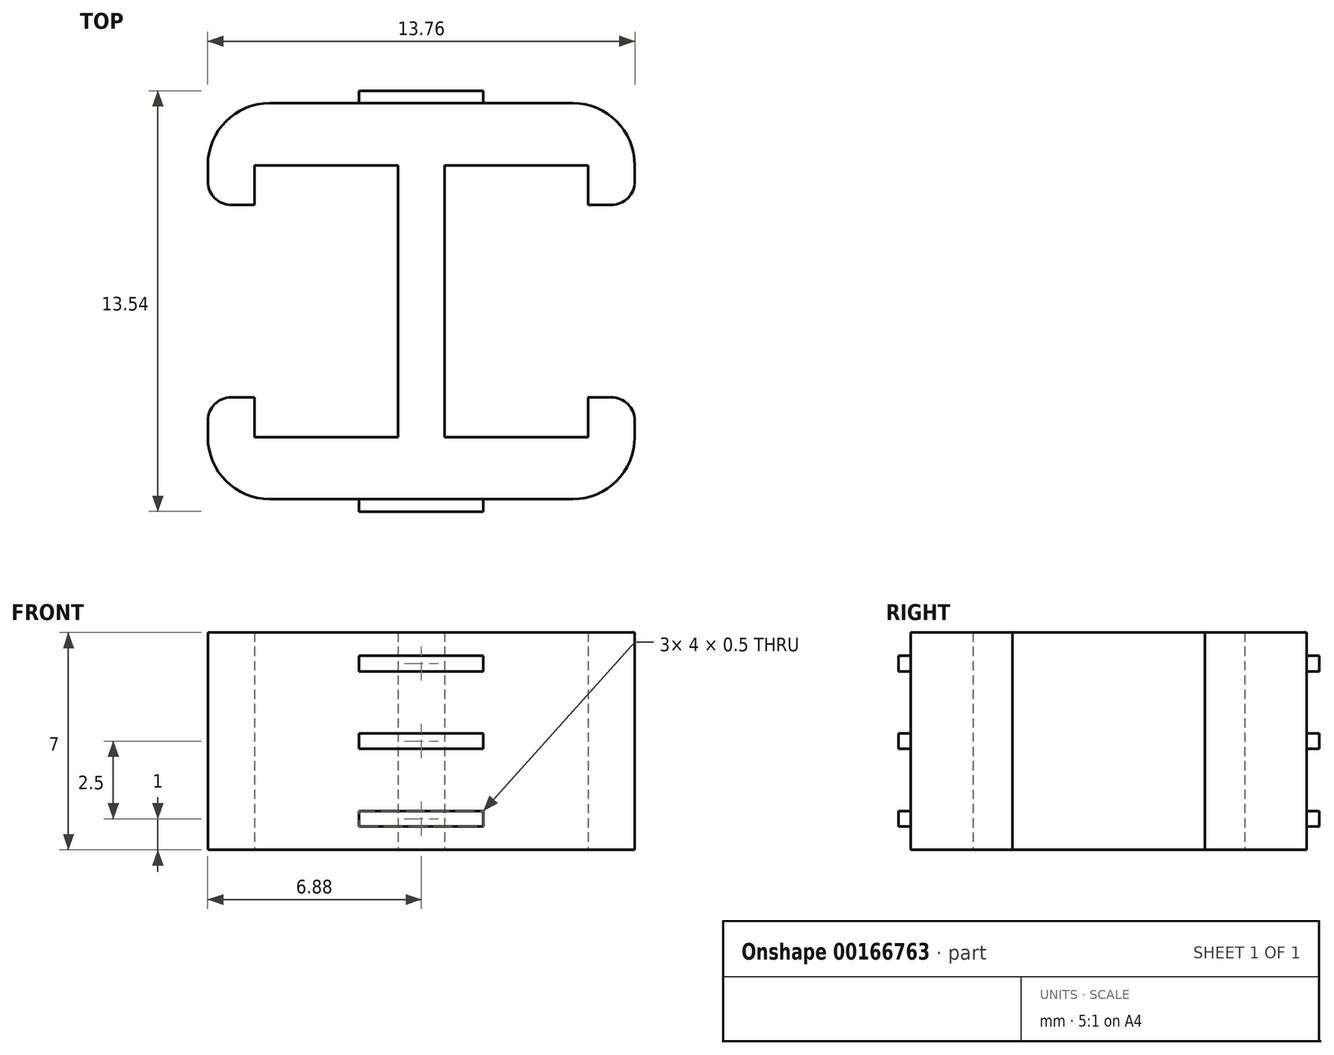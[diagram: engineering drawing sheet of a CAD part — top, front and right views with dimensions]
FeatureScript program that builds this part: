
annotation { "Feature Type Name" : "Feature", "Feature Type Description" : "" }
export const myFeature = defineFeature(function(context is Context, id is Id, definition is map)
    precondition{}
    {
        {
            var Q0;
            Q0=qCreatedBy(makeId("Top.planeOp"),FACE);
            var sketch = newSketch(context, id + "F0", { "sketchPlane" : qUnion([Q0])});
            skPoint(sketch, "E0.middle", {"position": v(0, 0) * mm});
            skLineSegment(sketch, "E1", {"start": v(0, 0) * mm, "end": v(0, 4.38) * mm, "construction": true});
            skLineSegment(sketch, "E2.bottom", {"start": v(0.75, -4.37) * mm, "end": v(-0.75, -4.37) * mm});
            skLineSegment(sketch, "E2.top", {"start": v(0.75, 4.38) * mm, "end": v(-0.75, 4.38) * mm});
            skLineSegment(sketch, "E2.left", {"start": v(0.75, -4.37) * mm, "end": v(0.75, 4.38) * mm});
            skLineSegment(sketch, "E3", {"start": v(-0.75, 4.38) * mm, "end": v(-0.75, -4.37) * mm});
            skLineSegment(sketch, "E4.bottom", {"start": v(-5.38, 6.38) * mm, "end": v(5.38, 6.38) * mm});
            skLineSegment(sketch, "E4.top", {"start": v(-5.38, 4.38) * mm, "end": v(5.38, 4.38) * mm});
            skLineSegment(sketch, "E4.left", {"start": v(-5.37, 6.38) * mm, "end": v(-5.37, 4.38) * mm});
            skLineSegment(sketch, "E4.right", {"start": v(5.38, 6.38) * mm, "end": v(5.38, 4.38) * mm});
            skLineSegment(sketch, "E5", {"start": v(0, 0) * mm, "end": v(7.23, 0) * mm, "construction": true});
            skLineSegment(sketch, "E6.bottom", {"start": v(5.38, 6.38) * mm, "end": v(6.88, 6.38) * mm});
            skLineSegment(sketch, "E6.top", {"start": v(5.38, 3.1) * mm, "end": v(6.88, 3.1) * mm});
            skLineSegment(sketch, "E6.left", {"start": v(5.38, 6.38) * mm, "end": v(5.38, 3.1) * mm});
            skLineSegment(sketch, "E6.right", {"start": v(6.88, 6.38) * mm, "end": v(6.88, 3.1) * mm});
            skLineSegment(sketch, "E7.MirrorCS", {"start": v(-5.38, 6.38) * mm, "end": v(-5.38, 4.38) * mm});
            skLineSegment(sketch, "E8.MirrorCS", {"start": v(-5.38, 6.38) * mm, "end": v(-6.88, 6.38) * mm});
            skLineSegment(sketch, "E9.MirrorCS", {"start": v(-6.88, 6.38) * mm, "end": v(-6.88, 3.1) * mm});
            skLineSegment(sketch, "E10.MirrorCS", {"start": v(-5.38, 6.38) * mm, "end": v(-5.38, 3.1) * mm});
            skLineSegment(sketch, "E11.MirrorCS", {"start": v(-5.38, 3.1) * mm, "end": v(-6.88, 3.1) * mm});
            skLineSegment(sketch, "E12.MirrorCS", {"start": v(-5.38, -6.38) * mm, "end": v(-5.38, -4.38) * mm});
            skLineSegment(sketch, "E13.MirrorCS", {"start": v(5.38, -6.38) * mm, "end": v(5.38, -4.38) * mm});
            skLineSegment(sketch, "E14.MirrorCS", {"start": v(0.75, -4.38) * mm, "end": v(-0.75, -4.38) * mm});
            skLineSegment(sketch, "E15.MirrorCS", {"start": v(-6.88, -6.38) * mm, "end": v(-6.88, -3.1) * mm});
            skLineSegment(sketch, "E16.MirrorCS", {"start": v(-5.38, -3.1) * mm, "end": v(-6.88, -3.1) * mm});
            skLineSegment(sketch, "E17.MirrorCS", {"start": v(5.38, -6.38) * mm, "end": v(5.38, -3.1) * mm});
            skLineSegment(sketch, "E18.MirrorCS", {"start": v(5.38, -3.1) * mm, "end": v(6.88, -3.1) * mm});
            skLineSegment(sketch, "E19.MirrorCS", {"start": v(5.38, -6.38) * mm, "end": v(6.88, -6.38) * mm});
            skLineSegment(sketch, "E20.MirrorCS", {"start": v(-5.38, -6.38) * mm, "end": v(-5.38, -3.1) * mm});
            skLineSegment(sketch, "E21.MirrorCS", {"start": v(6.88, -6.38) * mm, "end": v(6.88, -3.1) * mm});
            skLineSegment(sketch, "E22.MirrorCS", {"start": v(-5.38, -6.38) * mm, "end": v(-6.88, -6.38) * mm});
            skLineSegment(sketch, "E23.MirrorCS", {"start": v(-5.38, -4.38) * mm, "end": v(5.38, -4.38) * mm});
            skLineSegment(sketch, "E24.MirrorCS", {"start": v(-5.38, -6.38) * mm, "end": v(5.38, -6.38) * mm});
            skSolve(sketch);
        }
        {
            var Q0;
            Q0 = qSketchRegion(id + "F0", true);
            extrude(context, id + "F1", {"entities" : qUnion([Q0]), "depth" : 7 * mm});
        }
        {
            var Q0;
            Q0=makeQuery(id+"F1.opExtrude","SWEPT_EDGE",EDGE,{"disambiguationData":[OSD([sQuery(id+"F0.wireOp",EDGE,"E9.MirrorCS"),sQuery(id+"F0.wireOp",EDGE,"E11.MirrorCS")])]});
            var Q1;
            Q1=makeQuery(id+"F1.opExtrude","SWEPT_EDGE",EDGE,{"disambiguationData":[OSD([sQuery(id+"F0.wireOp",EDGE,"E6.top"),sQuery(id+"F0.wireOp",EDGE,"E6.right")])]});
            var Q2;
            Q2=makeQuery(id+"F1.opExtrude","SWEPT_EDGE",EDGE,{"disambiguationData":[OSD([sQuery(id+"F0.wireOp",EDGE,"E18.MirrorCS"),sQuery(id+"F0.wireOp",EDGE,"E21.MirrorCS")])]});
            var Q3;
            Q3=makeQuery(id+"F1.opExtrude","SWEPT_EDGE",EDGE,{"disambiguationData":[OSD([sQuery(id+"F0.wireOp",EDGE,"E15.MirrorCS"),sQuery(id+"F0.wireOp",EDGE,"E16.MirrorCS")])]});
            fillet(context, id + "F2", {"entities" : qUnion([Q0, Q1, Q2, Q3]), "radius" : .75 * mm, "tangentPropagation" : true, "allowEdgeOverflow" : false});
        }
        {
            var Q0;
            Q0=makeQuery(id+"F1.opExtrude","SWEPT_EDGE",EDGE,{"disambiguationData":[OSD([sQuery(id+"F0.wireOp",EDGE,"E15.MirrorCS"),sQuery(id+"F0.wireOp",EDGE,"E22.MirrorCS")])]});
            var Q1;
            Q1=makeQuery(id+"F1.opExtrude","SWEPT_EDGE",EDGE,{"disambiguationData":[OSD([sQuery(id+"F0.wireOp",EDGE,"E19.MirrorCS"),sQuery(id+"F0.wireOp",EDGE,"E21.MirrorCS")])]});
            var Q2;
            Q2=makeQuery(id+"F1.opExtrude","SWEPT_EDGE",EDGE,{"disambiguationData":[OSD([sQuery(id+"F0.wireOp",EDGE,"E6.bottom"),sQuery(id+"F0.wireOp",EDGE,"E6.right")])]});
            var Q3;
            Q3=makeQuery(id+"F1.opExtrude","SWEPT_EDGE",EDGE,{"disambiguationData":[OSD([sQuery(id+"F0.wireOp",EDGE,"E8.MirrorCS"),sQuery(id+"F0.wireOp",EDGE,"E9.MirrorCS")])]});
            fillet(context, id + "F3", {"entities" : qUnion([Q0, Q1, Q2, Q3]), "radius" : 2 * mm, "tangentPropagation" : true, "allowEdgeOverflow" : false});
        }
        {
            var Q0;
            Q0=makeQuery(id+"F1.opExtrude","SWEPT_FACE",FACE,{"disambiguationData":[OSD([sQuery(id+"F0.wireOp",EDGE,"E4.bottom"),sQuery(id+"F0.wireOp",EDGE,"E6.bottom"),sQuery(id+"F0.wireOp",EDGE,"E8.MirrorCS")])]});
            var sketch = newSketch(context, id + "F4", { "sketchPlane" : qUnion([Q0])});
            skLineSegment(sketch, "E25", {"start": v(0, 0) * mm, "end": v(0, 7) * mm, "construction": true});
            skLineSegment(sketch, "E26.bottom", {"start": v(-2, 3.75) * mm, "end": v(2, 3.75) * mm});
            skLineSegment(sketch, "E26.top", {"start": v(-2, 3.25) * mm, "end": v(2, 3.25) * mm});
            skLineSegment(sketch, "E26.left", {"start": v(-2, 3.75) * mm, "end": v(-2, 3.25) * mm});
            skLineSegment(sketch, "E26.right", {"start": v(2, 3.75) * mm, "end": v(2, 3.25) * mm});
            skPoint(sketch, "E26.middle", {"position": v(0, 3.5) * mm});
            skLineSegment(sketch, "E27.0.1.0", {"start": v(-2, 6.25) * mm, "end": v(2, 6.25) * mm});
            skPoint(sketch, "E27.0.1.1", {"position": v(0, 6) * mm});
            skLineSegment(sketch, "E27.0.1.2", {"start": v(-2, 5.75) * mm, "end": v(2, 5.75) * mm});
            skLineSegment(sketch, "E27.0.1.3", {"start": v(2, 6.25) * mm, "end": v(2, 5.75) * mm});
            skLineSegment(sketch, "E27.0.1.4", {"start": v(-2, 6.25) * mm, "end": v(-2, 5.75) * mm});
            skLineSegment(sketch, "E27.direction1", {"start": v(-2, 3.25) * mm, "end": v(3.96, 1.3) * mm, "construction": true});
            skLineSegment(sketch, "E27.direction2", {"start": v(-2, 3.25) * mm, "end": v(-2, 5.75) * mm, "construction": true});
            skLineSegment(sketch, "E28.0.1.0", {"start": v(-2, 0.75) * mm, "end": v(2, 0.75) * mm});
            skPoint(sketch, "E28.0.1.1", {"position": v(0, 1) * mm});
            skLineSegment(sketch, "E28.0.1.2", {"start": v(-2, 1.25) * mm, "end": v(2, 1.25) * mm});
            skLineSegment(sketch, "E28.0.1.3", {"start": v(2, 1.25) * mm, "end": v(2, 0.75) * mm});
            skLineSegment(sketch, "E28.0.1.4", {"start": v(-2, 1.25) * mm, "end": v(-2, 0.75) * mm});
            skLineSegment(sketch, "E28.direction1", {"start": v(-2, 3.25) * mm, "end": v(5.3, 3.25) * mm, "construction": true});
            skLineSegment(sketch, "E28.direction2", {"start": v(-2, 3.25) * mm, "end": v(-2, 0.75) * mm, "construction": true});
            skSolve(sketch);
        }
        {
            var Q0;
            Q0=makeQuery(id+"F4.imprint","IMPRINT",FACE,{"disambiguationData":[TD([[makeQuery(id+"F4.imprint","IMPRINT",EDGE,{"derivedFrom":sQuery(id+"F4.wireOp",EDGE,"E28.0.2.0")}),1.0]])]});
            var Q1;
            Q1=makeQuery(id+"F4.imprint","IMPRINT",FACE,{"disambiguationData":[TD([[makeQuery(id+"F4.imprint","IMPRINT",EDGE,{"derivedFrom":sQuery(id+"F4.wireOp",EDGE,"E28.0.1.0")}),1.0]])]});
            var Q2;
            Q2=makeQuery(id+"F4.imprint","IMPRINT",FACE,{"disambiguationData":[TD([[makeQuery(id+"F4.imprint","IMPRINT",EDGE,{"derivedFrom":sQuery(id+"F4.wireOp",EDGE,"E26.bottom")}),-1.0]])]});
            var Q3;
            Q3=makeQuery(id+"F4.imprint","IMPRINT",FACE,{"disambiguationData":[TD([[makeQuery(id+"F4.imprint","IMPRINT",EDGE,{"derivedFrom":sQuery(id+"F4.wireOp",EDGE,"E27.0.1.0")}),-1.0]])]});
            var Q4;
            Q4=makeQuery(id+"F4.imprint","IMPRINT",FACE,{"disambiguationData":[TD([[makeQuery(id+"F4.imprint","IMPRINT",EDGE,{"derivedFrom":sQuery(id+"F4.wireOp",EDGE,"E27.0.2.0")}),-1.0]])]});
            extrude(context, id + "F5", {"entities" : qUnion([Q0, Q1, Q2, Q3, Q4]), "operationType" : NewBodyOperationType.ADD, "depth" : .4 * mm});
        }
        {
            var Q0;
            Q0=makeQuery(id+"F1.opExtrude","SWEPT_FACE",FACE,{"disambiguationData":[OSD([sQuery(id+"F0.wireOp",EDGE,"E19.MirrorCS"),sQuery(id+"F0.wireOp",EDGE,"E22.MirrorCS"),sQuery(id+"F0.wireOp",EDGE,"E24.MirrorCS")])]});
            var sketch = newSketch(context, id + "F6", { "sketchPlane" : qUnion([Q0])});
            skLineSegment(sketch, "E29", {"start": v(0, -0.5) * mm, "end": v(0, 7.5) * mm, "construction": true});
            skLineSegment(sketch, "E30.bottom", {"start": v(-2, 3.75) * mm, "end": v(2, 3.75) * mm});
            skLineSegment(sketch, "E30.top", {"start": v(-2, 3.25) * mm, "end": v(2, 3.25) * mm});
            skLineSegment(sketch, "E30.left", {"start": v(-2, 3.75) * mm, "end": v(-2, 3.25) * mm});
            skLineSegment(sketch, "E30.right", {"start": v(2, 3.75) * mm, "end": v(2, 3.25) * mm});
            skPoint(sketch, "E30.middle", {"position": v(0, 3.5) * mm});
            skLineSegment(sketch, "E31.0.1.0", {"start": v(-2, 6.25) * mm, "end": v(2, 6.25) * mm});
            skPoint(sketch, "E31.0.1.1", {"position": v(0, 6) * mm});
            skLineSegment(sketch, "E31.0.1.2", {"start": v(-2, 5.75) * mm, "end": v(2, 5.75) * mm});
            skLineSegment(sketch, "E31.0.1.3", {"start": v(2, 6.25) * mm, "end": v(2, 5.75) * mm});
            skLineSegment(sketch, "E31.0.1.4", {"start": v(-2, 6.25) * mm, "end": v(-2, 5.75) * mm});
            skLineSegment(sketch, "E31.direction1", {"start": v(-2, 3.25) * mm, "end": v(-1.43, 3.06) * mm, "construction": true});
            skLineSegment(sketch, "E31.direction2", {"start": v(-2, 3.25) * mm, "end": v(-2, 5.75) * mm, "construction": true});
            skLineSegment(sketch, "E32.0.1.0", {"start": v(-2, 0.75) * mm, "end": v(2, 0.75) * mm});
            skPoint(sketch, "E32.0.1.1", {"position": v(0, 1) * mm});
            skLineSegment(sketch, "E32.0.1.2", {"start": v(-2, 1.25) * mm, "end": v(2, 1.25) * mm});
            skLineSegment(sketch, "E32.0.1.3", {"start": v(2, 1.25) * mm, "end": v(2, 0.75) * mm});
            skLineSegment(sketch, "E32.0.1.4", {"start": v(-2, 1.25) * mm, "end": v(-2, 0.75) * mm});
            skLineSegment(sketch, "E32.direction1", {"start": v(-2, 3.25) * mm, "end": v(-0.15, 3.25) * mm, "construction": true});
            skLineSegment(sketch, "E32.direction2", {"start": v(-2, 3.25) * mm, "end": v(-2, 0.75) * mm, "construction": true});
            skSolve(sketch);
        }
        {
            var Q0;
            Q0 = qSketchRegion(id + "F6", true);
            extrude(context, id + "F7", {"entities" : qUnion([Q0]), "operationType" : NewBodyOperationType.ADD, "depth" : .4 * mm});
        }
    });
